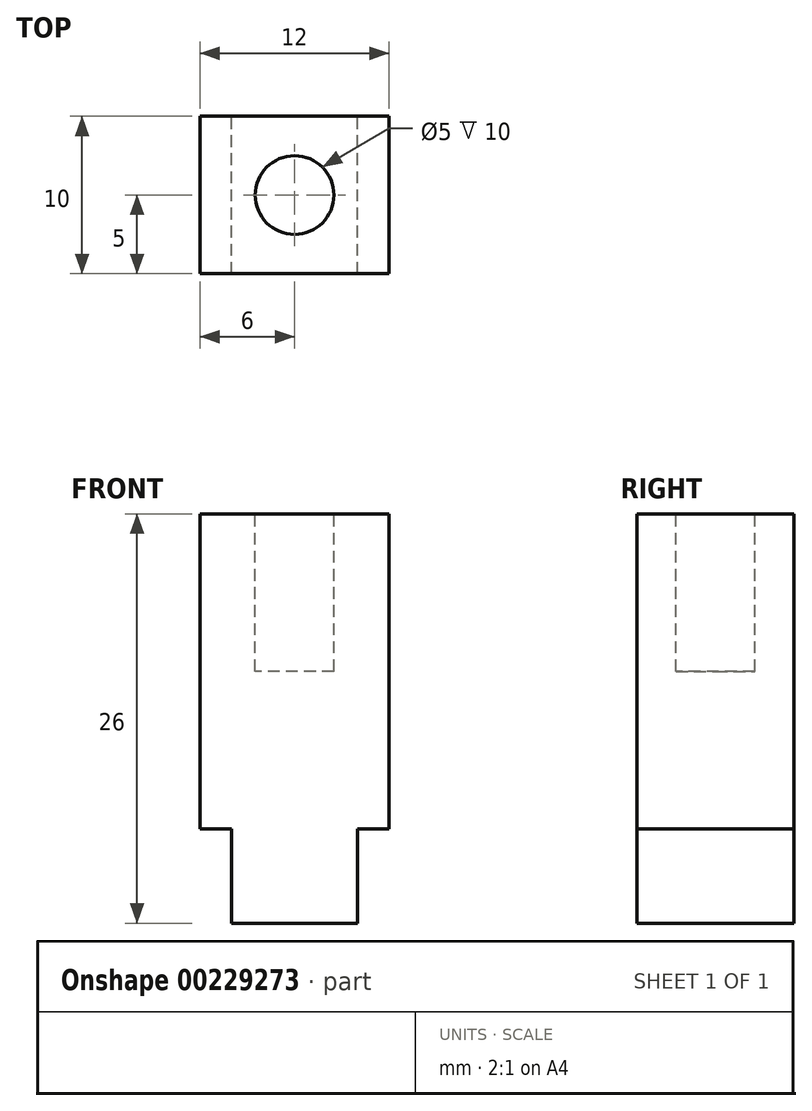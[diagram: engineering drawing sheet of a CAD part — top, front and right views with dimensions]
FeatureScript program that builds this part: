
annotation { "Feature Type Name" : "Feature", "Feature Type Description" : "" }
export const myFeature = defineFeature(function(context is Context, id is Id, definition is map)
    precondition{}
    {
        {
            var Q0;
            Q0=qCreatedBy(makeId("Front.planeOp"),FACE);
            var sketch = newSketch(context, id + "F0", { "sketchPlane" : qUnion([Q0])});
            skLineSegment(sketch, "E0.top", {"start": v(-4, -3) * mm, "end": v(4, -3) * mm});
            skLineSegment(sketch, "E0.left", {"start": v(-4, 3) * mm, "end": v(-4, -3) * mm});
            skLineSegment(sketch, "E0.right", {"start": v(4, 3) * mm, "end": v(4, -3) * mm});
            skPoint(sketch, "E0.middle", {"position": v(0, 0) * mm});
            skLineSegment(sketch, "E1", {"start": v(-6, 23) * mm, "end": v(6, 23) * mm});
            skLineSegment(sketch, "E2", {"start": v(-4, 3) * mm, "end": v(-6, 3) * mm});
            skLineSegment(sketch, "E3", {"start": v(-6, 3) * mm, "end": v(-6, 23) * mm});
            skLineSegment(sketch, "E4", {"start": v(6, 23) * mm, "end": v(6, 3) * mm});
            skLineSegment(sketch, "E5", {"start": v(6, 3) * mm, "end": v(4, 3) * mm});
            skSolve(sketch);
        }
        {
            var Q0;
            Q0 = qSketchRegion(id + "F0", true);
            extrude(context, id + "F1", {"entities" : qUnion([Q0]), "depth" : 10 * mm});
        }
        {
            var Q0;
            Q0=makeQuery(id+"F1.opExtrude","SWEPT_FACE",FACE,{"disambiguationData":[OSD([sQuery(id+"F0.wireOp",EDGE,"E1")])]});
            var sketch = newSketch(context, id + "F2", { "sketchPlane" : qUnion([Q0])});
            skCircle(sketch, "E6", {"center": v(0, -5) * mm, "radius": 2.5 * mm});
            skSolve(sketch);
        }
        {
            var Q0;
            Q0=makeQuery(id+"F2.imprint","IMPRINT",FACE,{"disambiguationData":[TD([[makeQuery(id+"F2.imprint","IMPRINT",EDGE,{"derivedFrom":sQuery(id+"F2.wireOp",EDGE,"E6")}),1.0]])]});
            var Q1;
            Q1=sQuery(id+"F2.wireOp",EDGE,"E6");
            extrude(context, id + "F3", {"entities" : qUnion([Q0]), "operationType" : NewBodyOperationType.REMOVE, "surfaceEntities" : qUnion([Q1]), "oppositeDirection" : true, "depth" : 10 * mm});
        }
    });
